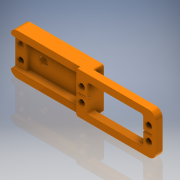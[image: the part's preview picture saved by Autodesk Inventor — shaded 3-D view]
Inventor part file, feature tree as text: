
AUTODESK INVENTOR PART (.ipt)
format: ipt  version: 2017 (Build 210142000, 142)  size: 269,824 bytes
history: native  units: mm
features: extrude x8, sketch x6, fillet x2
ambient origin geometry x8: Origin, YZ Plane, XZ Plane, XY Plane, X Axis, Y Axis, Z Axis, Center Point
bodies: Solid1 (feature_tree)
feature tree (16):
  extrude  "Extrusion1"  Depth=8.0mm
  sketch  "Sketch4"  dims[d2=5.0mm d3=49.5mm]
  extrude  "Extrusion3"  Depth=49.5mm
  sketch  "Sketch5"  dims[d4=49.5mm d5=2.0mm]
  extrude  "Extrusion4"  Depth=2.0mm
  extrude  "Extrusion5"  TaperAngle=0.0deg  [1 undecoded]
  extrude  "Extrusion6"  Depth=5.0mm
  fillet  "Fillet1"  Radius=4.0mm
  extrude  "Extrusion7"  Depth=2.0mm
  extrude  "Extrusion8"  Depth=2.0mm
  fillet  "Fillet2"  Radius=4.0mm
  extrude  "Extrusion9"  Depth=2.0mm
  sketch  "Sketch1"  dims[d0=10.0mm d1=8.0mm]
  sketch  "Sketch6"  dims[d6=30.0mm d7=0.0mm]
  sketch  "Sketch7"  dims[d19=5.0mm d20=5.0mm d22=4.0mm]
  sketch  "Sketch8"  dims[d23=4.5mm d25=2.75mm d26=2.75mm d27=4.0mm d28=30.0mm d29=0.0mm d30=5.0mm d31=5.0mm d33=4.5mm d34=4.0mm d35=2.75mm d36=2.75mm d37=30.0mm d38=0.0mm d39=5.0mm d40=0.0mm d41=6.5mm d42=1.2mm d43=2.0mm d44=0.0mm d45=5.0mm d46=4.2mm d47=10.0mm d48=10.0mm d49=0.0mm d50=40.5mm d51=40.5mm d52=2.5mm d53=0.0mm d54=1.5mm d55=6.2mm d56=2.0mm d57=0.0mm]
note: 1 required parameter value undecoded (feature->parameter linkage not recoverable at this tier; creation-order binding heuristic only, values carry confidence <= 0.55)
